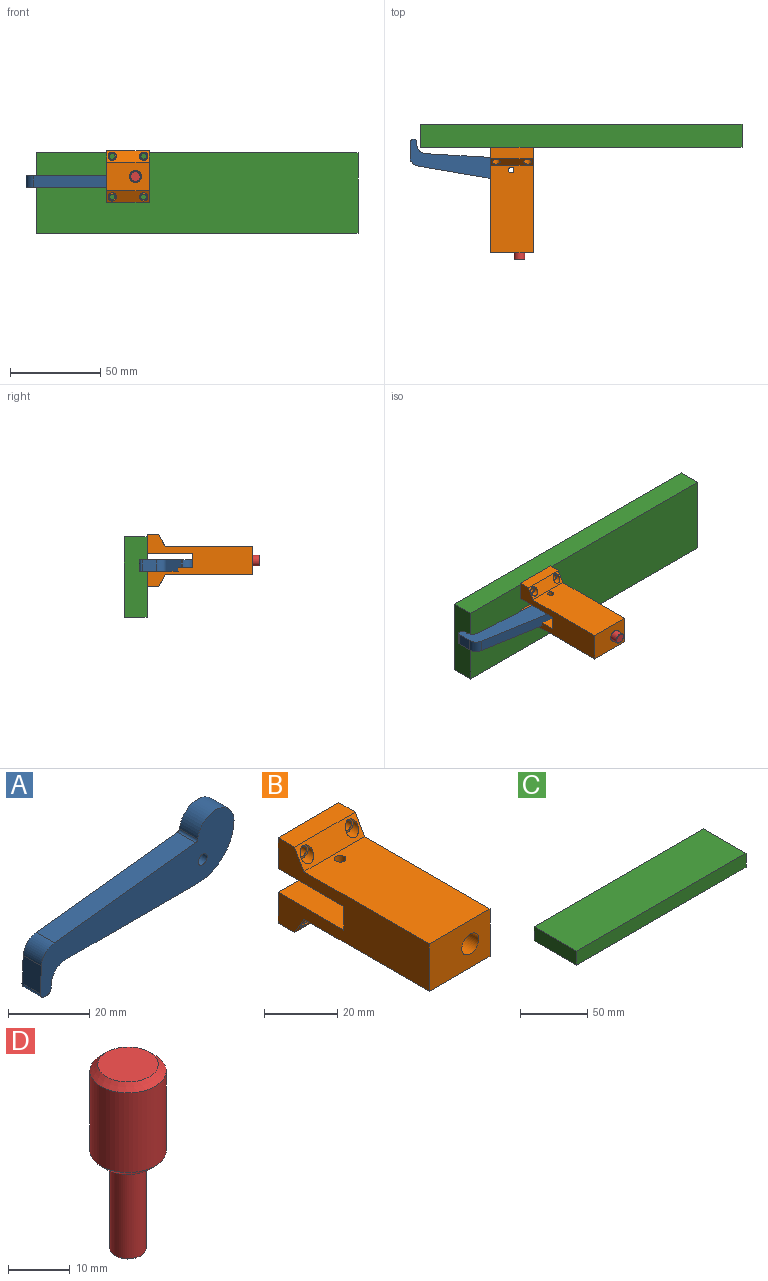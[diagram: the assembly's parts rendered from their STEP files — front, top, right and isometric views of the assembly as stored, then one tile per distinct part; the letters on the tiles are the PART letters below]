
ASSEMBLY  parts=4 mates=3
PART A: 15 faces, bbox 67.6x6.4x26.6 mm
  f0: plane 45.98x6.35mm, normal (0,0,-1), area 292mm2, adj f7,f8,f9,f11
  f1: cylinder r=6.35mm len=12.67mm, axis (0,1,0), area 122.8mm2, adj f7,f8,f9,f12
  f2: plane 49.35x6.35mm, normal (-0.11,0,0.99), area 315.4mm2, adj f7,f8,f10,f12
  f3: plane 8.13x6.35mm, normal (-1,0,0.05), area 51.7mm2, adj f7,f8,f10,f13
  f4: plane 6.35x0.76mm, normal (-0.05,0,-1), area 4.8mm2, adj f7,f8,f13,f14
  f5: cylinder r=1.59mm len=6.35mm, axis (0,1,0), area 63.3mm2, adj f7,f8
  f6: plane 6.35x1.27mm, normal (1,0,-0.05), area 8.1mm2, adj f7,f8,f11,f14
  f7: plane 67.63x26.58mm, normal (0,-1,0), area 734.2mm2, adj f0,f1,f2,f3,f4,f5,f6,f9
  f8: plane 67.63x26.58mm, normal (0,1,0), area 734.2mm2, adj f0,f1,f2,f3,f4,f5,f6,f9
  f9: cylinder r=12.7mm len=12.7mm, axis (0,1,0), area 126.7mm2, adj f0,f1,f7,f8
  f10: cylinder r=5.08mm len=6.35mm, axis (0,-1,0), area 45.3mm2, adj f2,f3,f7,f8
  f11: cylinder r=5.08mm len=6.35mm, axis (0,1,0), area 49mm2, adj f0,f6,f7,f8
  f12: cylinder r=0.76mm len=6.35mm, axis (0,1,0), area 6.6mm2, adj f1,f2,f7,f8
  f13: cylinder r=1.52mm len=6.35mm, axis (0,1,0), area 15.2mm2, adj f3,f4,f7,f8
  f14: cylinder r=1.52mm len=6.35mm, axis (0,1,0), area 15.2mm2, adj f4,f6,f7,f8
PART B: 36 faces, bbox 24.1x59x29.1 mm
  f0: plane 48.4x23.5mm, normal (0,0,1), area 1129.3mm2, adj f2,f3,f10,f18,f23
  f1: plane 48.4x23.5mm, normal (0,0,-1), area 1129.3mm2, adj f2,f3,f10,f19,f22
  f2: plane 58.42x28.58mm, normal (-1,0,0), area 831.3mm2, adj f0,f1,f5,f10,f11,f15,f16,f17
  f3: plane 58.42x28.58mm, normal (1,0,0), area 831.3mm2, adj f0,f1,f5,f10,f11,f12,f13,f14
  f4: cylinder r=6.35mm len=55.25mm, axis (0,-1,0), area 1758.7mm2, adj f5,f6,f11,f12,f13,f14,f15,f16
  f5: plane 23.5x10.35mm, normal (0,1,0), area 210.6mm2, adj f2,f3,f4,f13,f16,f20,f26,f27
  f6: plane 12.7x12.7mm, normal (0,1,0), area 64.6mm2, adj f4,f7
  f7: cylinder r=4.45mm len=9.53mm, axis (0,-1,0), area 266mm2, adj f6,f9
  f8: cylinder r=3.3mm len=12.7mm, axis (0,-1,0), area 263.5mm2, adj f9,f10
  f9: plane 8.89x8.89mm, normal (0,1,0), area 27.8mm2, adj f7,f8
  f10: plane 23.5x15.88mm, normal (0,-1,0), area 338.7mm2, adj f0,f1,f2,f3,f8
  f11: plane 23.5x10.35mm, normal (0,1,0), area 210.6mm2, adj f2,f3,f4,f12,f17,f21,f24,f25
  f12: plane 25.4x2.64mm, normal (0,0,-1), area 67mm2, adj f3,f4,f11,f14
  f13: plane 25.4x2.64mm, normal (0,0,1), area 67mm2, adj f3,f4,f5,f14
  f14: plane 7.87x2.64mm, normal (0,1,0), area 13.4mm2, adj f3,f4,f12,f13
  f15: plane 10.89x7.87mm, normal (0,1,0), area 78.4mm2, adj f2,f4,f16,f17
  f16: plane 25.4x10.89mm, normal (0,0,1), area 274mm2, adj f2,f4,f5,f15,f19
  f17: plane 25.4x10.89mm, normal (0,0,-1), area 274mm2, adj f2,f4,f11,f15,f18
  f18: cylinder r=1.59mm len=4mm, axis (0,0,1), area 33.3mm2, adj f0,f4,f17
  f19: cylinder r=1.59mm len=4mm, axis (0,0,1), area 33.3mm2, adj f1,f4,f16
  f20: plane 23.5x6.35mm, normal (0,0,-1), area 149.2mm2, adj f2,f3,f5,f22
  f21: plane 23.5x6.35mm, normal (0,0,1), area 149.2mm2, adj f2,f3,f11,f23
  f22: plane 24.05x6.91mm, normal (0,-0.87,-0.5), area 134.4mm2, adj f1,f2,f3,f20,f28,f30
  f23: plane 23.5x6.35mm, normal (0,-0.87,0.5), area 134.4mm2, adj f0,f2,f3,f21,f32,f34
  f24: cylinder r=1.59mm len=6.35mm, axis (0,1,0), area 63.3mm2, adj f11,f35
  f25: cylinder r=1.59mm len=6.35mm, axis (0,1,0), area 63.3mm2, adj f11,f33
  f26: cylinder r=1.59mm len=6.35mm, axis (0,1,0), area 63.3mm2, adj f5,f31
  f27: cylinder r=1.59mm len=6.35mm, axis (0,1,0), area 63.3mm2, adj f5,f29
  f28: cylinder r=2.29mm len=4.57mm, axis (0,1,0), area 25.3mm2, adj f22,f29
  f29: plane 4.57x4.57mm, normal (0,-1,0), area 8.5mm2, adj f27,f28
  f30: cylinder r=2.29mm len=4.57mm, axis (0,1,0), area 25.3mm2, adj f22,f31
  f31: plane 4.57x4.57mm, normal (0,-1,0), area 8.5mm2, adj f26,f30
  f32: cylinder r=2.29mm len=4.57mm, axis (0,1,0), area 25.3mm2, adj f23,f33
  f33: plane 4.57x4.57mm, normal (0,-1,0), area 8.5mm2, adj f25,f32
  f34: cylinder r=2.29mm len=4.57mm, axis (0,1,0), area 25.3mm2, adj f23,f35
  f35: plane 4.57x4.57mm, normal (0,-1,0), area 8.5mm2, adj f24,f34
PART C: 6 faces, bbox 177.8x44.5x12.7 mm
  f0: plane 177.8x44.45mm, normal (0,0,1), area 7903.2mm2, adj f1,f3,f4,f5
  f1: plane 44.45x12.7mm, normal (-1,0,0), area 564.5mm2, adj f0,f2,f4,f5
  f2: plane 177.8x44.45mm, normal (0,0,-1), area 7903.2mm2, adj f1,f3,f4,f5
  f3: plane 44.45x12.7mm, normal (1,0,0), area 564.5mm2, adj f0,f2,f4,f5
  f4: plane 177.8x12.7mm, normal (0,-1,0), area 2258.1mm2, adj f0,f1,f2,f3
  f5: plane 177.8x12.7mm, normal (0,1,0), area 2258.1mm2, adj f0,f1,f2,f3
PART D: 8 faces, bbox 12.3x12.3x36.6 mm
  f0: cylinder r=6.16mm len=15.75mm, axis (0,0,-1), area 609.5mm2, adj f5,f6
  f1: plane 9.78x9.78mm, normal (0,0,1), area 75.1mm2, adj f6
  f2: plane 9.78x9.78mm, normal (0,0,-1), area 48.3mm2, adj f3,f5
  f3: cylinder r=2.92mm len=18.03mm, axis (0,0,1), area 331mm2, adj f2,f7
  f4: plane 5.33x5.33mm, normal (0,0,-1), area 22.3mm2, adj f7
  f5: cone r=6.16mm half-angle=45deg, axis (0,0,1), area 62.3mm2, adj f0,f2
  f6: cone r=4.89mm half-angle=45deg, axis (0,0,-1), area 62.3mm2, adj f0,f1
  f7: cone r=2.67mm half-angle=45deg, axis (0,0,1), area 6.3mm2, adj f3,f4
PLACE A rot(axis=(1,-0.03,-0.03),90deg) t=(-0.03,45.72,-2.76)mm
PLACE B t=(4.54,0,0)mm
PLACE C rot(axis=(0,-0.71,-0.71),180deg) t=(38.83,64.77,-9.11)mm
PLACE D rot(axis=(-1,0,0),90deg) t=(4.54,14.28,0)mm
MATE fastened B.f5 <-> C.f2  axis (0,1,0) through (12.16,58.42,-9.11)mm
MATE revolute A.f5 <-> B.f18  axis (0,0,1) through (-0.03,45.72,-5.94)mm
MATE slider D.f3 <-> B.f8  axis (0,1,0) through (4.54,5.27,0)mm
